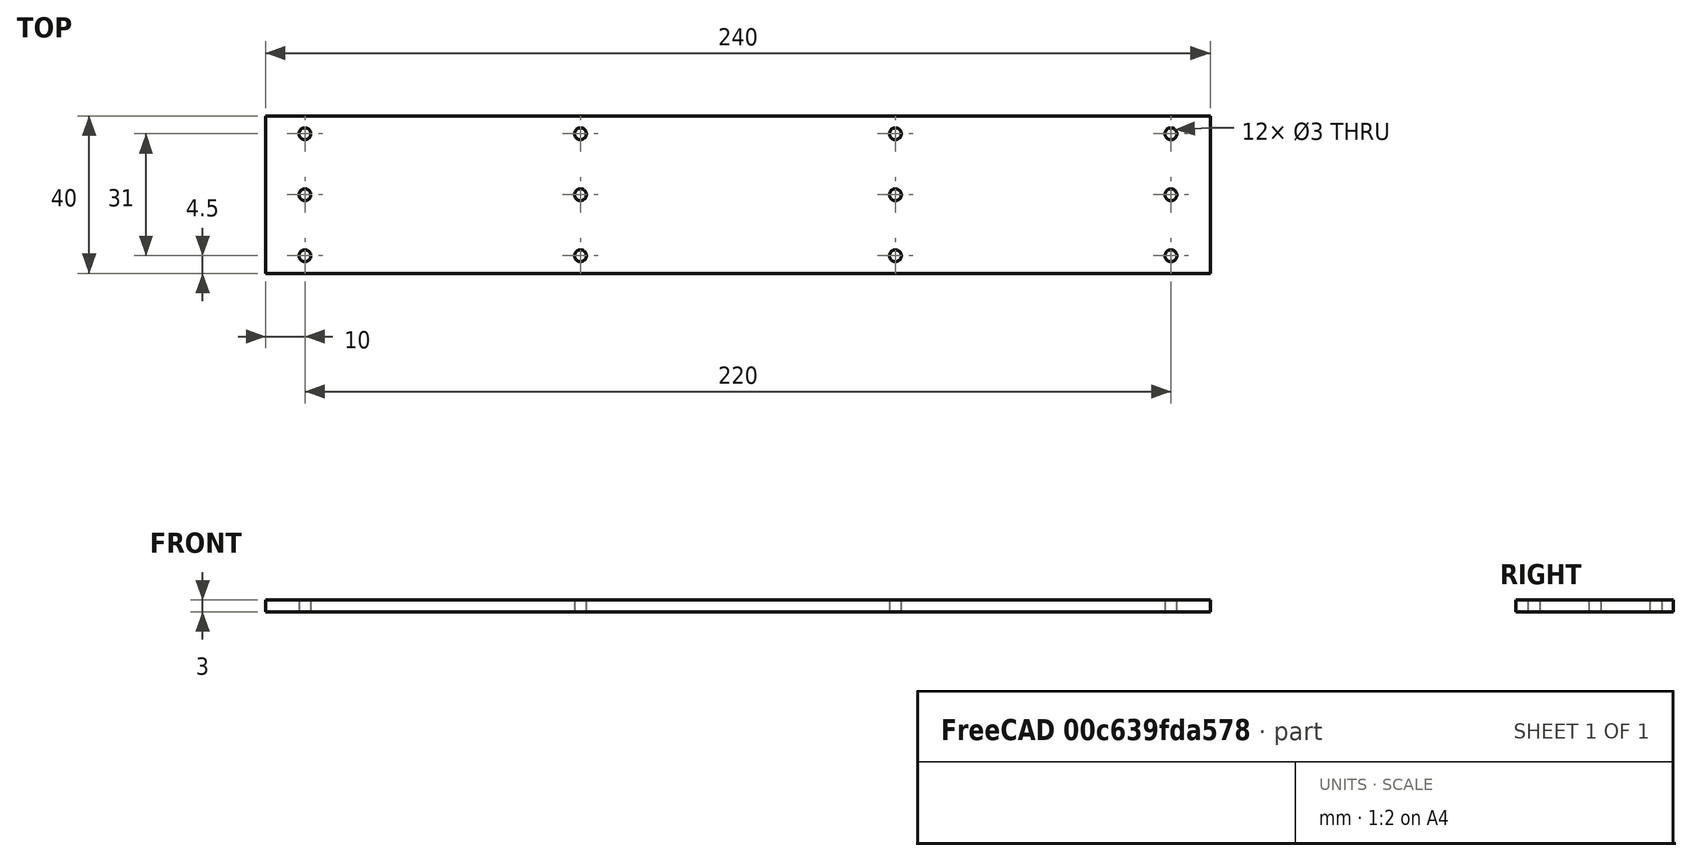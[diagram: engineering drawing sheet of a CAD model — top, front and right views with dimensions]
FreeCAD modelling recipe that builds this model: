
FCSTD DOCUMENT  (FreeCAD 0.14R3702 (Git))
Label: union
License: CC-BY 3.0
LicenseURL: http://creativecommons.org/licenses/by/3.0/
objects: Sketcher::SketchObject×1, PartDesign::Pad×1
note: 3 computed .brp shape members not serialized (recipe doc carries the construction recipe); baked Part::Feature solids carry a one-line shape summary decoded from their .brp

FEATURE [Sketcher::SketchObject] Sketch
  sketch-geometry (16):
    g0: LineSegment StartX=0 StartY=0 StartZ=0 EndX=240 EndY=0 EndZ=0
    g1: LineSegment StartX=240 StartY=0 StartZ=0 EndX=240 EndY=-40 EndZ=0
    g2: LineSegment StartX=240 StartY=-40 StartZ=0 EndX=0 EndY=-40 EndZ=0
    g3: LineSegment StartX=0 StartY=-40 StartZ=0 EndX=0 EndY=0 EndZ=0
    g4: Circle CenterX=10 CenterY=-4.5 CenterZ=0 NormalX=0 NormalY=0 NormalZ=1 Radius=1.5
    g5: Circle CenterX=10 CenterY=-20 CenterZ=0 NormalX=0 NormalY=0 NormalZ=1 Radius=1.5
    g6: Circle CenterX=10 CenterY=-35.5 CenterZ=0 NormalX=0 NormalY=0 NormalZ=1 Radius=1.5
    g7: Circle CenterX=80 CenterY=-4.5 CenterZ=0 NormalX=0 NormalY=0 NormalZ=1 Radius=1.5
    g8: Circle CenterX=80 CenterY=-20 CenterZ=0 NormalX=0 NormalY=0 NormalZ=1 Radius=1.5
    g9: Circle CenterX=80 CenterY=-35.5 CenterZ=0 NormalX=0 NormalY=0 NormalZ=1 Radius=1.5
    g10: Circle CenterX=160 CenterY=-4.5 CenterZ=0 NormalX=0 NormalY=0 NormalZ=1 Radius=1.5
    g11: Circle CenterX=160 CenterY=-20 CenterZ=0 NormalX=0 NormalY=0 NormalZ=1 Radius=1.5
    g12: Circle CenterX=160 CenterY=-35.5 CenterZ=0 NormalX=0 NormalY=0 NormalZ=1 Radius=1.5
    g13: Circle CenterX=230 CenterY=-4.5 CenterZ=0 NormalX=0 NormalY=0 NormalZ=1 Radius=1.5
    g14: Circle CenterX=230 CenterY=-20 CenterZ=0 NormalX=0 NormalY=0 NormalZ=1 Radius=1.5
    g15: Circle CenterX=230 CenterY=-35.5 CenterZ=0 NormalX=0 NormalY=0 NormalZ=1 Radius=1.5
  constraints (47):
    c: Coincident(g0,g1)
    c: Coincident(g1,g2)
    c: Coincident(g2,g3)
    c: Coincident(g3,g0)
    c: Horizontal(g0)
    c: Horizontal(g2)
    c: Vertical(g1)
    c: Vertical(g3)
    c: Coincident(g0,g-1)
    c: Distance(g0) = 240
    c: Distance(g1) = 40
    c: Radius(g4) = 1.5
    c: Distance(g4,g0) = 4.5
    c: Distance(g4,g3) = 10
    c: Distance(g5,g3) = 10
    c: Distance(g6,g3) = 10
    c: Distance(g5,g0) = 20
    c: Distance(g6,g2) = 4.5
    c: Radius(g5) = 1.5
    c: Radius(g6) = 1.5
    c: DistanceY(g4,g7) = 0
    c: DistanceY(g8,g5) = 0
    c: DistanceY(g6,g9) = 0
    c: Distance(g7,g3) = 80
    c: Radius(g7) = 1.5
    c: Radius(g8) = 1.5
    c: Radius(g9) = 1.5
    c: DistanceX(g8,g7) = 0
    c: DistanceX(g9,g8) = 0
    c: DistanceY(g12,g9) = 0
    c: DistanceY(g11,g8) = 0
    c: DistanceY(g10,g7) = 0
    c: DistanceY(g13,g10) = 0
    c: DistanceY(g14,g11) = 0
    c: DistanceY(g15,g12) = 0
    c: Distance(g13,g1) = 10
    c: DistanceX(g14,g13) = 0
    c: DistanceX(g15,g14) = 0
    c: Distance(g10,g1) = 80
    c: DistanceX(g11,g10) = 0
    c: DistanceX(g12,g11) = 0
    c: Radius(g10) = 1.5
    c: Radius(g11) = 1.5
    c: Radius(g12) = 1.5
    c: Radius(g13) = 1.5
    c: Radius(g14) = 1.5
    c: Radius(g15) = 1.5
FEATURE [PartDesign::Pad] Pad
  Length = 3
  Length2 = 100
  Sketch = -> Sketch
  Type = 0
